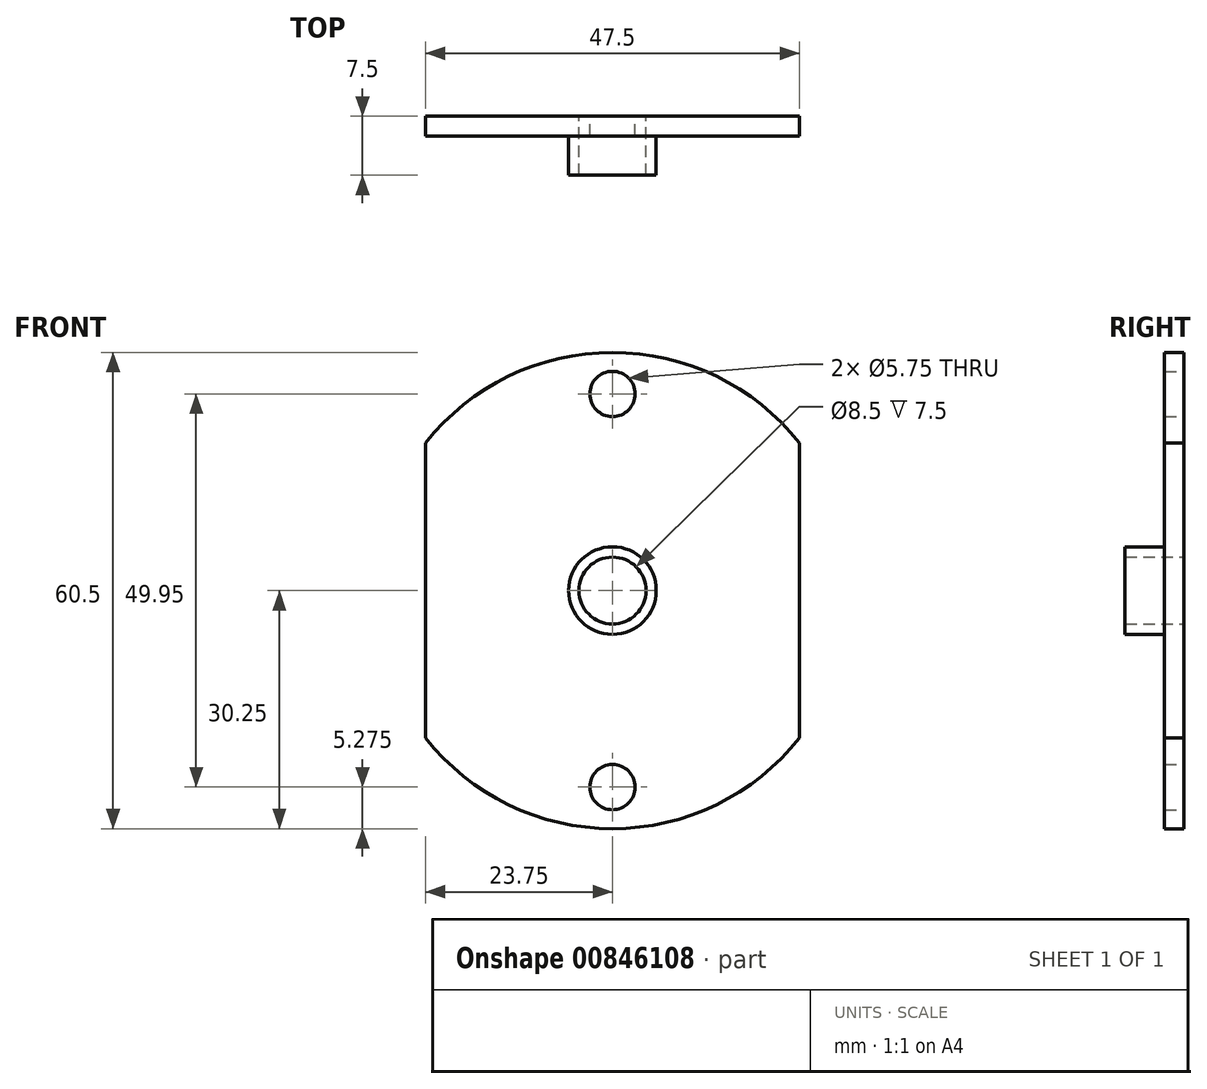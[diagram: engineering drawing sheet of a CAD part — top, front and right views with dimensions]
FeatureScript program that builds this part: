
annotation { "Feature Type Name" : "Feature", "Feature Type Description" : "" }
export const myFeature = defineFeature(function(context is Context, id is Id, definition is map)
    precondition{}
    {
        {
            var Q0;
            Q0=qCreatedBy(makeId("Front.planeOp"),FACE);
            var sketch = newSketch(context, id + "F0", { "sketchPlane" : qUnion([Q0])});
            skArc(sketch, "E0", {"start": v(23.75, 18.73) * mm, "mid": v(0, 30.25) * mm, "end": v(-23.75, 18.73) * mm});
            skLineSegment(sketch, "E1.left", {"start": v(23.75, -18.73) * mm, "end": v(23.75, 18.73) * mm});
            skLineSegment(sketch, "E1.right", {"start": v(-23.75, -18.73) * mm, "end": v(-23.75, 18.73) * mm});
            skPoint(sketch, "E2.orphan", {"position": v(23.75, 36.82) * mm});
            skPoint(sketch, "E3.orphan", {"position": v(-23.75, 36.82) * mm});
            skPoint(sketch, "E1.bottom.start.orphan", {"position": v(23.75, -36.82) * mm});
            skPoint(sketch, "E4.orphan", {"position": v(-23.75, -36.82) * mm});
            skArc(sketch, "E5.trimOffspring", {"start": v(-23.75, -18.73) * mm, "mid": v(0, -30.25) * mm, "end": v(23.75, -18.73) * mm});
            skCircle(sketch, "E6", {"center": v(0, 24.98) * mm, "radius": 2.88 * mm});
            skCircle(sketch, "E7", {"center": v(0, -24.98) * mm, "radius": 2.88 * mm});
            skCircle(sketch, "E8", {"center": v(0, 0) * mm, "radius": 4.25 * mm});
            skSolve(sketch);
        }
        {
            var Q0;
            Q0=makeQuery(id+"F0.imprint","IMPRINT",FACE,{"disambiguationData":[TD([[makeQuery(id+"F0.imprint","IMPRINT",EDGE,{"derivedFrom":sQuery(id+"F0.wireOp",EDGE,"E0")}),1.0]])]});
            extrude(context, id + "F1", {"entities" : qUnion([Q0]), "depth" : 2.5 * mm, "offsetDistance" : 25 * mm});
        }
        {
            var Q0;
            Q0=makeQuery(id+"F1.opExtrude","CAP_FACE",FACE,{"disambiguationData":[OSD([sQuery(id+"F0.wireOp",EDGE,"E0"),sQuery(id+"F0.wireOp",EDGE,"E1.left"),sQuery(id+"F0.wireOp",EDGE,"E1.right"),sQuery(id+"F0.wireOp",EDGE,"E5.trimOffspring"),sQuery(id+"F0.wireOp",EDGE,"E6"),sQuery(id+"F0.wireOp",EDGE,"E7")])],"isStart":false});
            var sketch = newSketch(context, id + "F2", { "sketchPlane" : qUnion([Q0])});
            skCircle(sketch, "E9", {"center": v(0, 0) * mm, "radius": 4.25 * mm});
            skCircle(sketch, "E10", {"center": v(0, 0) * mm, "radius": 5.55 * mm});
            skSolve(sketch);
        }
        {
            var Q0;
            Q0 = qSketchRegion(id + "F2", true);
            extrude(context, id + "F3", {"entities" : qUnion([Q0]), "operationType" : NewBodyOperationType.ADD, "depth" : 5 * mm, "offsetDistance" : 25 * mm});
        }
    });
